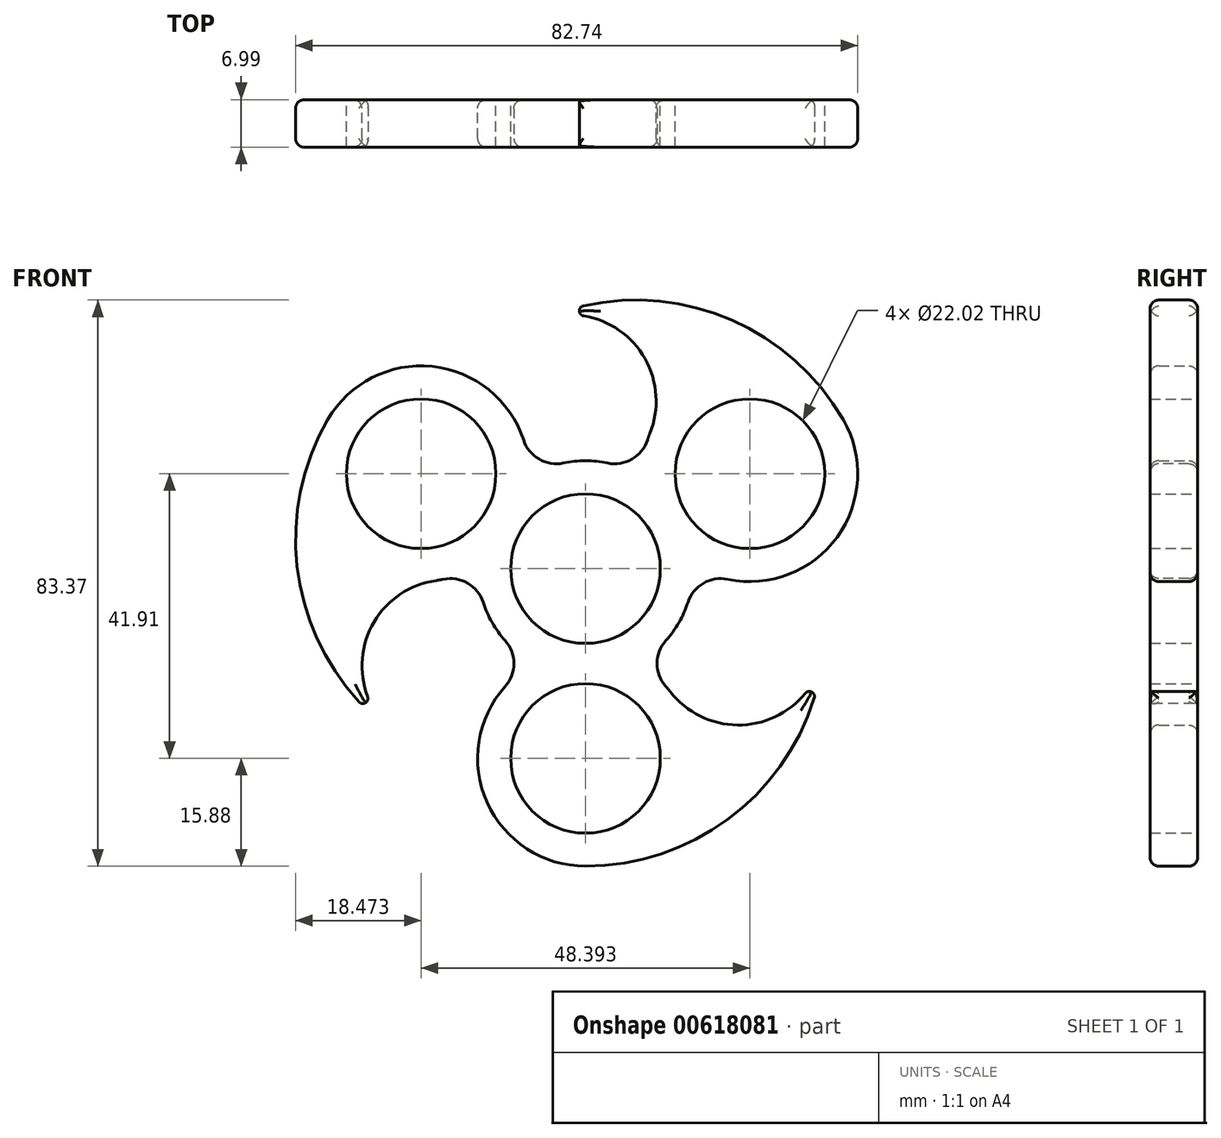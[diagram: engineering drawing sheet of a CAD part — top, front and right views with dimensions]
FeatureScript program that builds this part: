
annotation { "Feature Type Name" : "Feature", "Feature Type Description" : "" }
export const myFeature = defineFeature(function(context is Context, id is Id, definition is map)
    precondition{}
    {
        {
            var Q0;
            Q0=qCreatedBy(makeId("Front.planeOp"),FACE);
            var sketch = newSketch(context, id + "F0", { "sketchPlane" : qUnion([Q0])});
            skCircle(sketch, "E0", {"center": v(0, -27.94) * mm, "radius": 15.88 * mm});
            skArc(sketch, "E1", {"start": v(0, -43.82) * mm, "mid": v(23.93, -34.46) * mm, "end": v(35.17, -11.35) * mm});
            skLineSegment(sketch, "E2", {"start": v(-5.9, -41.26) * mm, "end": v(-5.9, -41.26) * mm});
            skCircle(sketch, "E3", {"center": v(0, 0) * mm, "radius": 11.01 * mm});
            skLineSegment(sketch, "E4", {"start": v(0, -27.94) * mm, "end": v(0, 0) * mm});
            skArc(sketch, "E5", {"start": v(12.5, -18.16) * mm, "mid": v(26.16, -22.5) * mm, "end": v(35.17, -11.35) * mm});
            skArc(sketch, "E6.1.0", {"start": v(37.94, 21.9) * mm, "mid": v(17.88, 37.95) * mm, "end": v(-7.75, 36.13) * mm});
            skLineSegment(sketch, "E6.1.1", {"start": v(24.2, 13.97) * mm, "end": v(0, 0) * mm});
            skArc(sketch, "E6.1.2", {"start": v(9.48, 19.91) * mm, "mid": v(6.4, 33.9) * mm, "end": v(-7.75, 36.13) * mm});
            skCircle(sketch, "E6.1.3", {"center": v(24.2, 13.97) * mm, "radius": 15.88 * mm});
            skArc(sketch, "E6.2.0", {"start": v(-37.94, 21.9) * mm, "mid": v(-41.8, -3.5) * mm, "end": v(-27.42, -24.78) * mm});
            skLineSegment(sketch, "E6.2.1", {"start": v(-24.2, 13.97) * mm, "end": v(0, 0) * mm});
            skArc(sketch, "E6.2.2", {"start": v(-21.98, -1.75) * mm, "mid": v(-32.57, -11.4) * mm, "end": v(-27.42, -24.78) * mm});
            skCircle(sketch, "E6.2.3", {"center": v(-24.2, 13.97) * mm, "radius": 15.88 * mm});
            skCircle(sketch, "E7", {"center": v(0, 0) * mm, "radius": 15.88 * mm});
            skCircle(sketch, "E8", {"center": v(24.2, 13.97) * mm, "radius": 11.01 * mm});
            skCircle(sketch, "E9", {"center": v(-24.2, 13.97) * mm, "radius": 11.01 * mm});
            skCircle(sketch, "E10", {"center": v(0, -27.94) * mm, "radius": 11.01 * mm});
            skSolve(sketch);
        }
        {
            var Q0;
            Q0 = qSketchRegion(id + "F0", true);
            extrude(context, id + "F1", {"entities" : qUnion([Q0]), "depth" : 7 * mm, "offsetDistance" : 25.4 * mm});
        }
        {
            var Q0;
            {var subQ0=sQuery(id+"F0.wireOp",EDGE,"E7");var subQ1=sQuery(id+"F0.wireOp",EDGE,"E6.2.3");Q0=makeQuery(id+"F1.opExtrude","SWEPT_EDGE",EDGE,{"disambiguationData":[OSD([subQ1,subQ0]),TDD([makeQuery(id+"F0.imprint","INTERSECT",VERTEX,{"disambiguationData":[OD(0.0)],"derivedFrom":[subQ1,subQ0]})])]});}
            var Q1;
            {var subQ0=sQuery(id+"F0.wireOp",EDGE,"E7");var subQ1=sQuery(id+"F0.wireOp",EDGE,"E0");Q1=makeQuery(id+"F1.opExtrude","SWEPT_EDGE",EDGE,{"disambiguationData":[OSD([subQ1,subQ0]),TDD([makeQuery(id+"F0.imprint","INTERSECT",VERTEX,{"disambiguationData":[OD(1.0)],"derivedFrom":[subQ1,subQ0]})])]});}
            var Q2;
            {var subQ0=sQuery(id+"F0.wireOp",EDGE,"E7");var subQ1=sQuery(id+"F0.wireOp",EDGE,"E0");Q2=makeQuery(id+"F1.opExtrude","SWEPT_EDGE",EDGE,{"disambiguationData":[OSD([subQ1,subQ0]),TDD([makeQuery(id+"F0.imprint","INTERSECT",VERTEX,{"disambiguationData":[OD(0.0)],"derivedFrom":[subQ1,subQ0]})])]});}
            var Q3;
            {var subQ0=sQuery(id+"F0.wireOp",EDGE,"E7");var subQ1=sQuery(id+"F0.wireOp",EDGE,"E6.1.3");Q3=makeQuery(id+"F1.opExtrude","SWEPT_EDGE",EDGE,{"disambiguationData":[OSD([subQ1,subQ0]),TDD([makeQuery(id+"F0.imprint","INTERSECT",VERTEX,{"disambiguationData":[OD(1.0)],"derivedFrom":[subQ1,subQ0]})])]});}
            var Q4;
            {var subQ0=sQuery(id+"F0.wireOp",EDGE,"E7");var subQ1=sQuery(id+"F0.wireOp",EDGE,"E6.1.3");Q4=makeQuery(id+"F1.opExtrude","SWEPT_EDGE",EDGE,{"disambiguationData":[OSD([subQ1,subQ0]),TDD([makeQuery(id+"F0.imprint","INTERSECT",VERTEX,{"disambiguationData":[OD(0.0)],"derivedFrom":[subQ1,subQ0]})])]});}
            var Q5;
            {var subQ0=sQuery(id+"F0.wireOp",EDGE,"E7");var subQ1=sQuery(id+"F0.wireOp",EDGE,"E6.2.3");Q5=makeQuery(id+"F1.opExtrude","SWEPT_EDGE",EDGE,{"disambiguationData":[OSD([subQ1,subQ0]),TDD([makeQuery(id+"F0.imprint","INTERSECT",VERTEX,{"disambiguationData":[OD(1.0)],"derivedFrom":[subQ1,subQ0]})])]});}
            fillet(context, id + "F2", {"entities" : qUnion([Q0, Q1, Q2, Q3, Q4, Q5]), "radius" : 5.08 * mm, "tangentPropagation" : true, "allowEdgeOverflow" : false});
        }
        {
            var Q0;
            Q0=makeQuery(id+"F1.opExtrude","CAP_EDGE",EDGE,{"disambiguationData":[OSD([sQuery(id+"F0.wireOp",EDGE,"E6.1.0")])],"isStart":false});
            var Q1;
            Q1=makeQuery(id+"F1.opExtrude","CAP_EDGE",EDGE,{"disambiguationData":[OSD([sQuery(id+"F0.wireOp",EDGE,"E6.1.2")])],"isStart":false});
            var Q2;
            {var subQ0=sQuery(id+"F0.wireOp",EDGE,"E6.1.3");Q2=makeQuery(id+"F1.opExtrude","CAP_EDGE",EDGE,{"disambiguationData":[OSD([subQ0]),TDD([makeQuery(id+"F0.imprint","IMPRINT",EDGE,{"disambiguationData":[TD([[makeQuery(id+"F0.imprint","INTERSECT",VERTEX,{"derivedFrom":[sQuery(id+"F0.wireOp",EDGE,"E6.1.2"),subQ0]}),-1.0]])],"derivedFrom":subQ0})])],"isStart":false});}
            var Q3;
            {var subQ0=sQuery(id+"F0.wireOp",EDGE,"E7");Q3=makeQuery(id+"F1.opExtrude","CAP_EDGE",EDGE,{"disambiguationData":[OSD([subQ0]),TDD([makeQuery(id+"F0.imprint","IMPRINT",EDGE,{"disambiguationData":[TD([[makeQuery(id+"F0.imprint","INTERSECT",VERTEX,{"disambiguationData":[OD(0.0)],"derivedFrom":[sQuery(id+"F0.wireOp",EDGE,"E6.1.3"),subQ0]}),-1.0]])],"derivedFrom":subQ0})])],"isStart":false});}
            var Q4;
            {var subQ0=sQuery(id+"F0.wireOp",EDGE,"E6.2.3");Q4=makeQuery(id+"F1.opExtrude","CAP_EDGE",EDGE,{"disambiguationData":[OSD([subQ0]),TDD([makeQuery(id+"F0.imprint","IMPRINT",EDGE,{"disambiguationData":[TD([[makeQuery(id+"F0.imprint","INTERSECT",VERTEX,{"derivedFrom":[sQuery(id+"F0.wireOp",EDGE,"E6.2.0"),subQ0]}),1.0]])],"derivedFrom":subQ0})])],"isStart":false});}
            var Q5;
            Q5=makeQuery(id+"F1.opExtrude","CAP_EDGE",EDGE,{"disambiguationData":[OSD([sQuery(id+"F0.wireOp",EDGE,"E6.2.0")])],"isStart":false});
            var Q6;
            Q6=makeQuery(id+"F1.opExtrude","CAP_EDGE",EDGE,{"disambiguationData":[OSD([sQuery(id+"F0.wireOp",EDGE,"E6.2.2")])],"isStart":false});
            var Q7;
            {var subQ0=sQuery(id+"F0.wireOp",EDGE,"E6.2.3");Q7=makeQuery(id+"F1.opExtrude","CAP_EDGE",EDGE,{"disambiguationData":[OSD([subQ0]),TDD([makeQuery(id+"F0.imprint","IMPRINT",EDGE,{"disambiguationData":[TD([[makeQuery(id+"F0.imprint","INTERSECT",VERTEX,{"derivedFrom":[sQuery(id+"F0.wireOp",EDGE,"E6.2.2"),subQ0]}),-1.0]])],"derivedFrom":subQ0})])],"isStart":false});}
            var Q8;
            {var subQ0=sQuery(id+"F0.wireOp",EDGE,"E7");Q8=makeQuery(id+"F1.opExtrude","CAP_EDGE",EDGE,{"disambiguationData":[OSD([subQ0]),TDD([makeQuery(id+"F0.imprint","IMPRINT",EDGE,{"disambiguationData":[TD([[makeQuery(id+"F0.imprint","INTERSECT",VERTEX,{"disambiguationData":[OD(1.0)],"derivedFrom":[sQuery(id+"F0.wireOp",EDGE,"E0"),subQ0]}),1.0]])],"derivedFrom":subQ0})])],"isStart":false});}
            var Q9;
            {var subQ0=sQuery(id+"F0.wireOp",EDGE,"E0");Q9=makeQuery(id+"F1.opExtrude","CAP_EDGE",EDGE,{"disambiguationData":[OSD([subQ0]),TDD([makeQuery(id+"F0.imprint","IMPRINT",EDGE,{"disambiguationData":[TD([[makeQuery(id+"F0.imprint","INTERSECT",VERTEX,{"derivedFrom":[subQ0,sQuery(id+"F0.wireOp",EDGE,"E1")]}),1.0]])],"derivedFrom":subQ0})])],"isStart":false});}
            var Q10;
            Q10=makeQuery(id+"F1.opExtrude","CAP_EDGE",EDGE,{"disambiguationData":[OSD([sQuery(id+"F0.wireOp",EDGE,"E1")])],"isStart":false});
            var Q11;
            Q11=makeQuery(id+"F1.opExtrude","CAP_EDGE",EDGE,{"disambiguationData":[OSD([sQuery(id+"F0.wireOp",EDGE,"E5")])],"isStart":false});
            var Q12;
            {var subQ0=sQuery(id+"F0.wireOp",EDGE,"E0");Q12=makeQuery(id+"F1.opExtrude","CAP_EDGE",EDGE,{"disambiguationData":[OSD([subQ0]),TDD([makeQuery(id+"F0.imprint","IMPRINT",EDGE,{"disambiguationData":[TD([[makeQuery(id+"F0.imprint","INTERSECT",VERTEX,{"derivedFrom":[subQ0,sQuery(id+"F0.wireOp",EDGE,"E5")]}),-1.0]])],"derivedFrom":subQ0})])],"isStart":false});}
            var Q13;
            {var subQ0=sQuery(id+"F0.wireOp",EDGE,"E7");Q13=makeQuery(id+"F1.opExtrude","CAP_EDGE",EDGE,{"disambiguationData":[OSD([subQ0]),TDD([makeQuery(id+"F0.imprint","IMPRINT",EDGE,{"disambiguationData":[TD([[makeQuery(id+"F0.imprint","INTERSECT",VERTEX,{"disambiguationData":[OD(0.0)],"derivedFrom":[sQuery(id+"F0.wireOp",EDGE,"E0"),subQ0]}),-1.0]])],"derivedFrom":subQ0})])],"isStart":false});}
            var Q14;
            {var subQ0=sQuery(id+"F0.wireOp",EDGE,"E6.1.3");Q14=makeQuery(id+"F1.opExtrude","CAP_EDGE",EDGE,{"disambiguationData":[OSD([subQ0]),TDD([makeQuery(id+"F0.imprint","IMPRINT",EDGE,{"disambiguationData":[TD([[makeQuery(id+"F0.imprint","INTERSECT",VERTEX,{"derivedFrom":[sQuery(id+"F0.wireOp",EDGE,"E6.1.0"),subQ0]}),1.0]])],"derivedFrom":subQ0})])],"isStart":false});}
            var Q15;
            {var subQ0=sQuery(id+"F0.wireOp",EDGE,"E6.2.3");Q15=makeQuery(id+"F1.opExtrude","CAP_EDGE",EDGE,{"disambiguationData":[OSD([subQ0]),TDD([makeQuery(id+"F0.imprint","IMPRINT",EDGE,{"disambiguationData":[TD([[makeQuery(id+"F0.imprint","INTERSECT",VERTEX,{"derivedFrom":[sQuery(id+"F0.wireOp",EDGE,"E6.2.0"),subQ0]}),1.0]])],"derivedFrom":subQ0})])],"isStart":true});}
            var Q16;
            Q16=makeQuery(id+"F1.opExtrude","CAP_EDGE",EDGE,{"disambiguationData":[OSD([sQuery(id+"F0.wireOp",EDGE,"E6.2.0")])],"isStart":true});
            var Q17;
            {var subQ0=sQuery(id+"F0.wireOp",EDGE,"E7");Q17=makeQuery(id+"F1.opExtrude","CAP_EDGE",EDGE,{"disambiguationData":[OSD([subQ0]),TDD([makeQuery(id+"F0.imprint","IMPRINT",EDGE,{"disambiguationData":[TD([[makeQuery(id+"F0.imprint","INTERSECT",VERTEX,{"disambiguationData":[OD(1.0)],"derivedFrom":[sQuery(id+"F0.wireOp",EDGE,"E0"),subQ0]}),1.0]])],"derivedFrom":subQ0})])],"isStart":true});}
            var Q18;
            {var subQ0=sQuery(id+"F0.wireOp",EDGE,"E6.2.3");Q18=makeQuery(id+"F1.opExtrude","CAP_EDGE",EDGE,{"disambiguationData":[OSD([subQ0]),TDD([makeQuery(id+"F0.imprint","IMPRINT",EDGE,{"disambiguationData":[TD([[makeQuery(id+"F0.imprint","INTERSECT",VERTEX,{"derivedFrom":[sQuery(id+"F0.wireOp",EDGE,"E6.2.2"),subQ0]}),-1.0]])],"derivedFrom":subQ0})])],"isStart":true});}
            var Q19;
            Q19=makeQuery(id+"F1.opExtrude","CAP_EDGE",EDGE,{"disambiguationData":[OSD([sQuery(id+"F0.wireOp",EDGE,"E6.2.2")])],"isStart":true});
            var Q20;
            {var subQ0=sQuery(id+"F0.wireOp",EDGE,"E0");Q20=makeQuery(id+"F1.opExtrude","CAP_EDGE",EDGE,{"disambiguationData":[OSD([subQ0]),TDD([makeQuery(id+"F0.imprint","IMPRINT",EDGE,{"disambiguationData":[TD([[makeQuery(id+"F0.imprint","INTERSECT",VERTEX,{"derivedFrom":[subQ0,sQuery(id+"F0.wireOp",EDGE,"E1")]}),1.0]])],"derivedFrom":subQ0})])],"isStart":true});}
            var Q21;
            Q21=makeQuery(id+"F1.opExtrude","CAP_EDGE",EDGE,{"disambiguationData":[OSD([sQuery(id+"F0.wireOp",EDGE,"E1")])],"isStart":true});
            var Q22;
            Q22=makeQuery(id+"F1.opExtrude","CAP_EDGE",EDGE,{"disambiguationData":[OSD([sQuery(id+"F0.wireOp",EDGE,"E5")])],"isStart":true});
            var Q23;
            {var subQ0=sQuery(id+"F0.wireOp",EDGE,"E7");Q23=makeQuery(id+"F1.opExtrude","CAP_EDGE",EDGE,{"disambiguationData":[OSD([subQ0]),TDD([makeQuery(id+"F0.imprint","IMPRINT",EDGE,{"disambiguationData":[TD([[makeQuery(id+"F0.imprint","INTERSECT",VERTEX,{"disambiguationData":[OD(0.0)],"derivedFrom":[sQuery(id+"F0.wireOp",EDGE,"E0"),subQ0]}),-1.0]])],"derivedFrom":subQ0})])],"isStart":true});}
            var Q24;
            {var subQ0=sQuery(id+"F0.wireOp",EDGE,"E6.1.3");Q24=makeQuery(id+"F1.opExtrude","CAP_EDGE",EDGE,{"disambiguationData":[OSD([subQ0]),TDD([makeQuery(id+"F0.imprint","IMPRINT",EDGE,{"disambiguationData":[TD([[makeQuery(id+"F0.imprint","INTERSECT",VERTEX,{"derivedFrom":[sQuery(id+"F0.wireOp",EDGE,"E6.1.0"),subQ0]}),1.0]])],"derivedFrom":subQ0})])],"isStart":true});}
            var Q25;
            Q25=makeQuery(id+"F1.opExtrude","CAP_EDGE",EDGE,{"disambiguationData":[OSD([sQuery(id+"F0.wireOp",EDGE,"E6.1.0")])],"isStart":true});
            var Q26;
            Q26=makeQuery(id+"F1.opExtrude","CAP_EDGE",EDGE,{"disambiguationData":[OSD([sQuery(id+"F0.wireOp",EDGE,"E6.1.2")])],"isStart":true});
            var Q27;
            {var subQ0=sQuery(id+"F0.wireOp",EDGE,"E7");Q27=makeQuery(id+"F1.opExtrude","CAP_EDGE",EDGE,{"disambiguationData":[OSD([subQ0]),TDD([makeQuery(id+"F0.imprint","IMPRINT",EDGE,{"disambiguationData":[TD([[makeQuery(id+"F0.imprint","INTERSECT",VERTEX,{"disambiguationData":[OD(0.0)],"derivedFrom":[sQuery(id+"F0.wireOp",EDGE,"E6.1.3"),subQ0]}),-1.0]])],"derivedFrom":subQ0})])],"isStart":true});}
            var Q28;
            {var subQ0=sQuery(id+"F0.wireOp",EDGE,"E6.1.3");Q28=makeQuery(id+"F1.opExtrude","CAP_EDGE",EDGE,{"disambiguationData":[OSD([subQ0]),TDD([makeQuery(id+"F0.imprint","IMPRINT",EDGE,{"disambiguationData":[TD([[makeQuery(id+"F0.imprint","INTERSECT",VERTEX,{"derivedFrom":[sQuery(id+"F0.wireOp",EDGE,"E6.1.2"),subQ0]}),-1.0]])],"derivedFrom":subQ0})])],"isStart":true});}
            fillet(context, id + "F3", {"entities" : qUnion([Q0, Q1, Q2, Q3, Q4, Q5, Q6, Q7, Q8, Q9, Q10, Q11, Q12, Q13, Q14, Q15, Q16, Q17, Q18, Q19, Q20, Q21, Q22, Q23, Q24, Q25, Q26, Q27, Q28]), "radius" : 1.27 * mm, "tangentPropagation" : true, "allowEdgeOverflow" : false});
        }
        {
            var Q0;
            Q0=makeQuery(id+"F1.opExtrude","SWEPT_EDGE",EDGE,{"disambiguationData":[OSD([sQuery(id+"F0.wireOp",EDGE,"E6.1.0"),sQuery(id+"F0.wireOp",EDGE,"E6.1.2")])]});
            var Q1;
            Q1=makeQuery(id+"F1.opExtrude","SWEPT_EDGE",EDGE,{"disambiguationData":[OSD([sQuery(id+"F0.wireOp",EDGE,"E1"),sQuery(id+"F0.wireOp",EDGE,"E5")])]});
            var Q2;
            Q2=makeQuery(id+"F1.opExtrude","SWEPT_EDGE",EDGE,{"disambiguationData":[OSD([sQuery(id+"F0.wireOp",EDGE,"E6.2.0"),sQuery(id+"F0.wireOp",EDGE,"E6.2.2")])]});
            fillet(context, id + "F4", {"entities" : qUnion([Q0, Q1, Q2]), "radius" : 0.76 * mm, "tangentPropagation" : true, "allowEdgeOverflow" : false});
        }
    });
